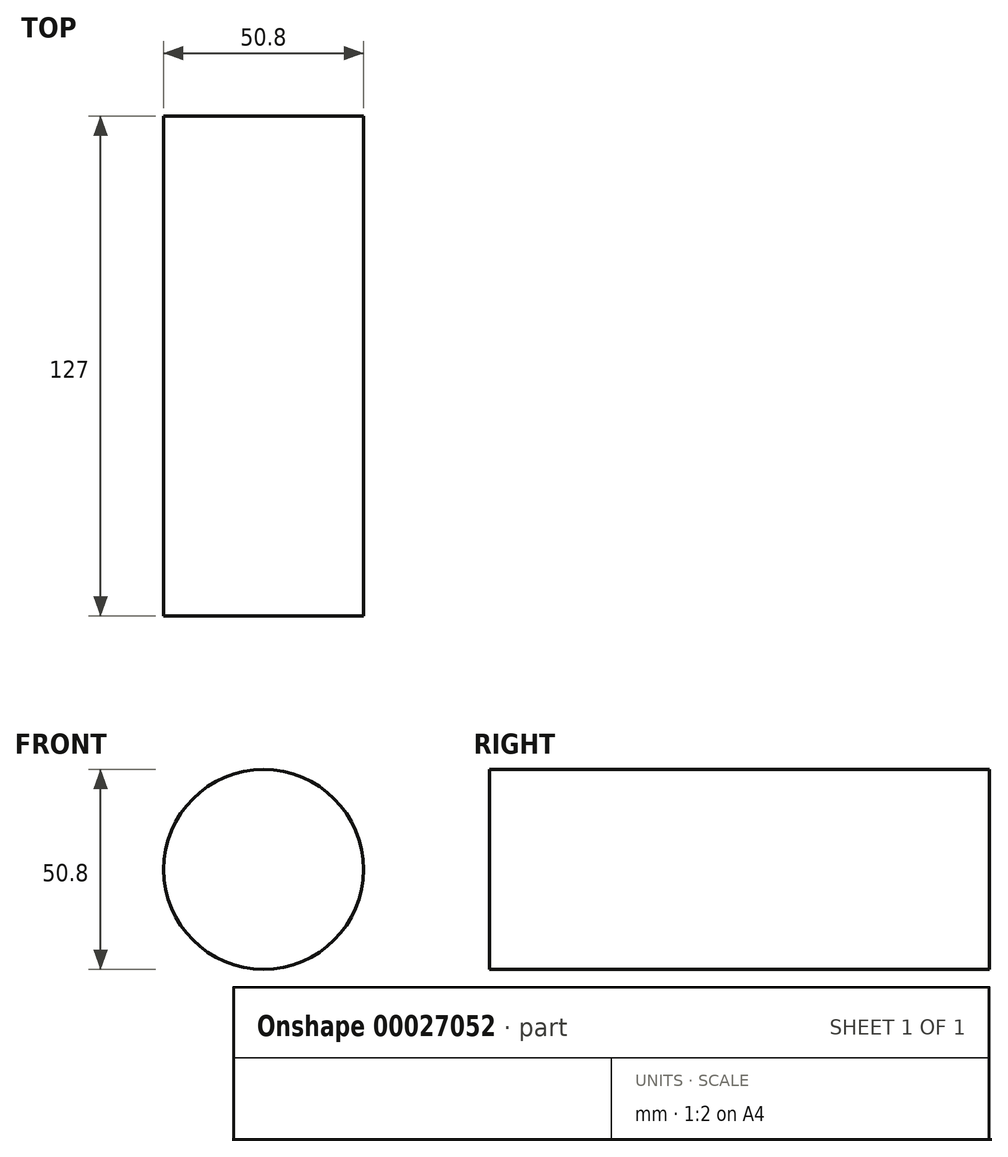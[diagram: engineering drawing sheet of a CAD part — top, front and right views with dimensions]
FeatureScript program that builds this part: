
annotation { "Feature Type Name" : "Feature", "Feature Type Description" : "" }
export const myFeature = defineFeature(function(context is Context, id is Id, definition is map)
    precondition{}
    {
        {
            var Q0;
            Q0=qCreatedBy(makeId("Front.planeOp"),FACE);
            var sketch = newSketch(context, id + "F0", { "sketchPlane" : qUnion([Q0])});
            skCircle(sketch, "E0", {"center": v(0, 0) * mm, "radius": 25.4 * mm});
            skSolve(sketch);
        }
        {
            var Q0;
            Q0 = qSketchRegion(id + "F0", true);
            extrude(context, id + "F1", {"entities" : qUnion([Q0]), "oppositeDirection" : true, "depth" : 127 * mm});
        }
    });
